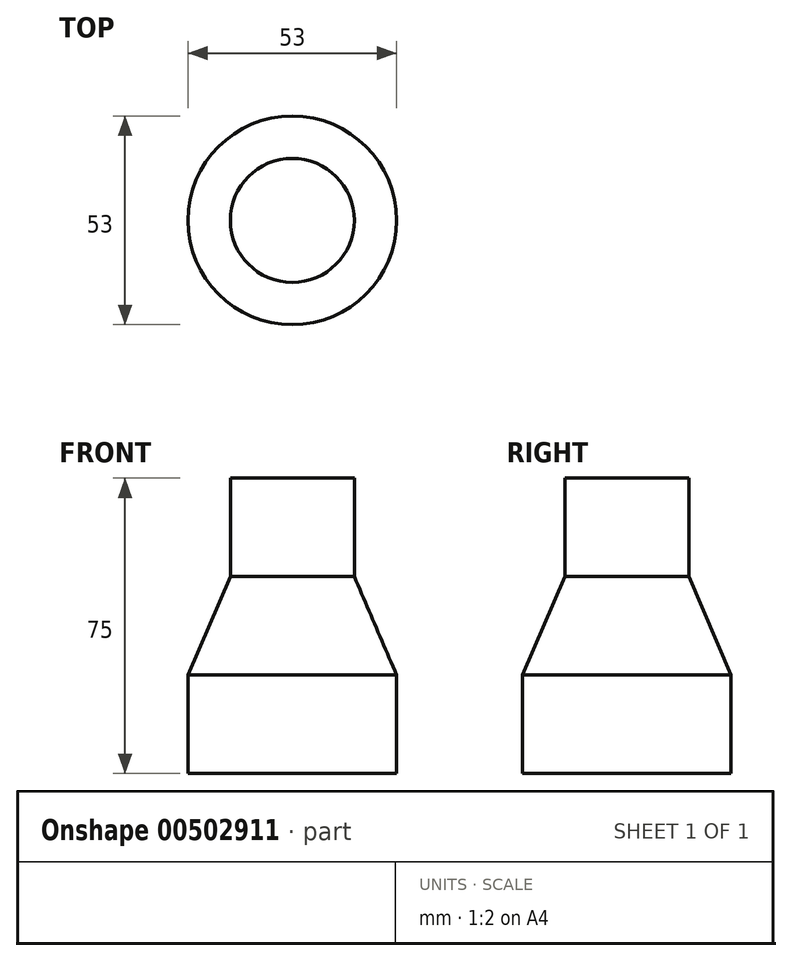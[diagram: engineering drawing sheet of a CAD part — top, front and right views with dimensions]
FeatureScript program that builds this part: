
annotation { "Feature Type Name" : "Feature", "Feature Type Description" : "" }
export const myFeature = defineFeature(function(context is Context, id is Id, definition is map)
    precondition{}
    {
        {
            var Q0;
            Q0=qCreatedBy(makeId("Top.planeOp"),FACE);
            var sketch = newSketch(context, id + "F0", { "sketchPlane" : qUnion([Q0])});
            skCircle(sketch, "E0", {"center": v(0, 0) * mm, "radius": 26.5 * mm});
            skSolve(sketch);
        }
        {
            var Q0;
            Q0=makeQuery(id+"F0.imprint","IMPRINT",FACE,{"disambiguationData":[TD([[makeQuery(id+"F0.imprint","IMPRINT",EDGE,{"derivedFrom":sQuery(id+"F0.wireOp",EDGE,"E0")}),1.0]])]});
            cPlane(context, id + "F1", {"entities" : qUnion([Q0]), "cplaneType" : CPlaneType.OFFSET, "offset" : 25 * mm, "width" : 150 * mm, "height" : 150 * mm});
        }
        {
            var Q0;
            Q0=qCreatedBy(id+"F1.planeOp",FACE);
            var sketch = newSketch(context, id + "F2", { "sketchPlane" : qUnion([Q0])});
            skCircle(sketch, "E1", {"center": v(0, 0) * mm, "radius": 15.75 * mm});
            skSolve(sketch);
        }
        {
            var Q0;
            Q0=makeQuery(id+"F2.imprint","IMPRINT",FACE,{"disambiguationData":[TD([[makeQuery(id+"F2.imprint","IMPRINT",EDGE,{"derivedFrom":sQuery(id+"F2.wireOp",EDGE,"E1")}),1.0]])]});
            var Q1;
            Q1=makeQuery(id+"F0.imprint","IMPRINT",FACE,{"disambiguationData":[TD([[makeQuery(id+"F0.imprint","IMPRINT",EDGE,{"derivedFrom":sQuery(id+"F0.wireOp",EDGE,"E0")}),1.0]])]});
            loft(context, id + "F3", {"sheetProfilesArray" : [{ "sheetProfileEntities" : qUnion([Q0]) }, { "sheetProfileEntities" : qUnion([Q1]) }]});
        }
        {
            var Q0;
            Q0=makeQuery(id+"F3.opLoft","CAP_FACE",FACE,{"disambiguationData":[OSD([makeQuery(id+"F2.imprint","IMPRINT",FACE,{"disambiguationData":[TD([[makeQuery(id+"F2.imprint","IMPRINT",EDGE,{"derivedFrom":sQuery(id+"F2.wireOp",EDGE,"E1")}),1.0]])]})])],"isStart":true});
            extrude(context, id + "F4", {"entities" : qUnion([Q0]), "operationType" : NewBodyOperationType.ADD, "depth" : 25 * mm});
        }
        {
            var Q0;
            Q0=makeQuery(id+"F3.opLoft","CAP_FACE",FACE,{"disambiguationData":[OSD([makeQuery(id+"F0.imprint","IMPRINT",FACE,{"disambiguationData":[TD([[makeQuery(id+"F0.imprint","IMPRINT",EDGE,{"derivedFrom":sQuery(id+"F0.wireOp",EDGE,"E0")}),1.0]])]})])],"isStart":true});
            extrude(context, id + "F5", {"entities" : qUnion([Q0]), "operationType" : NewBodyOperationType.ADD, "depth" : 25 * mm});
        }
    });
